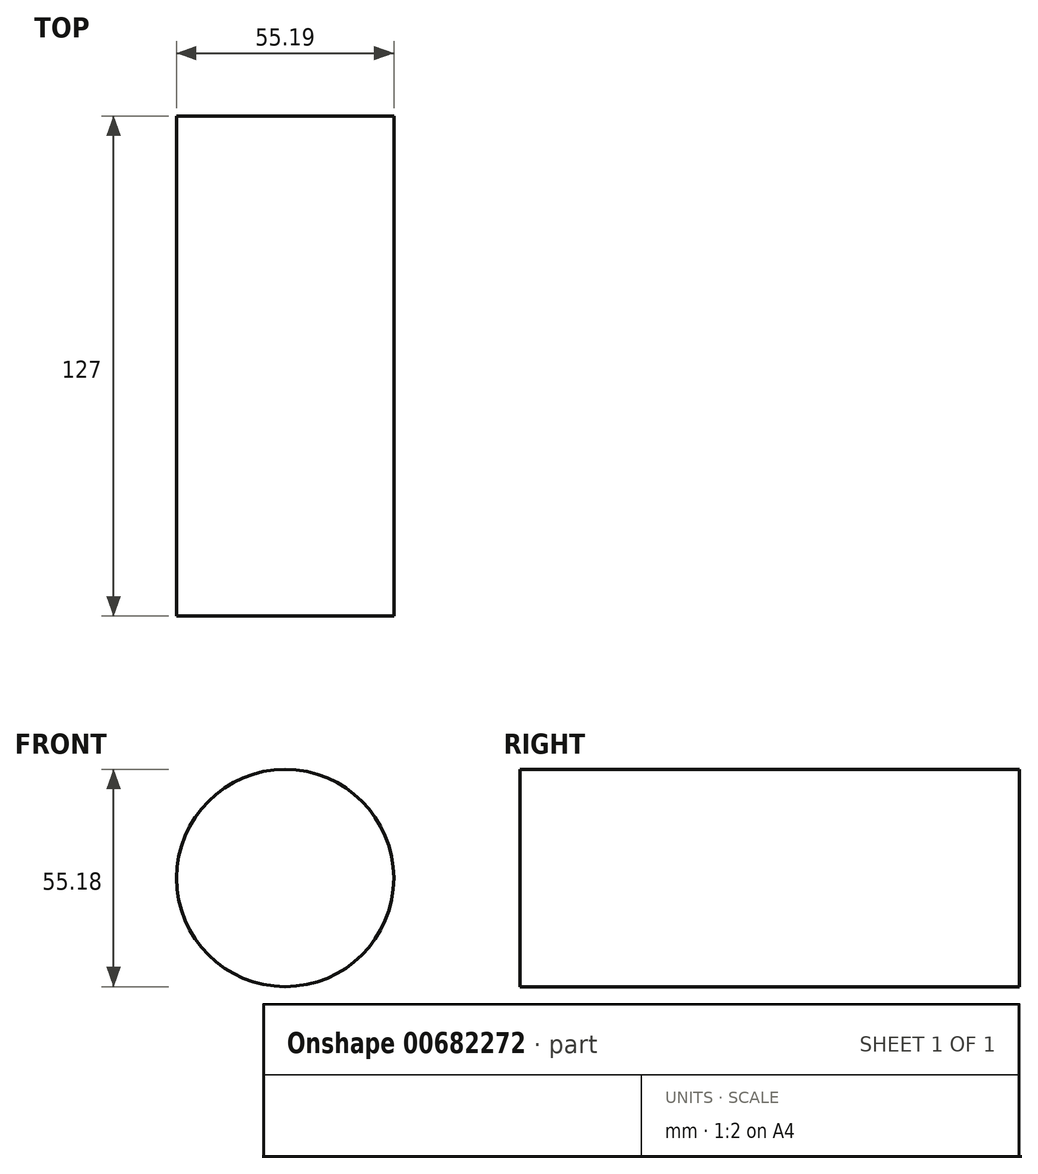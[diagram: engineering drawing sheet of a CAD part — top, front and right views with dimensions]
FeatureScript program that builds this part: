
annotation { "Feature Type Name" : "Feature", "Feature Type Description" : "" }
export const myFeature = defineFeature(function(context is Context, id is Id, definition is map)
    precondition{}
    {
        {
            var Q0;
            Q0=qCreatedBy(makeId("Front.planeOp"),FACE);
            var sketch = newSketch(context, id + "F0", { "sketchPlane" : qUnion([Q0])});
            skCircle(sketch, "E0", {"center": v(1.32, 0) * mm, "radius": 27.6 * mm});
            skSolve(sketch);
        }
        {
            var Q0;
            Q0=makeQuery(id+"F0.imprint","IMPRINT",FACE,{"disambiguationData":[TD([[makeQuery(id+"F0.imprint","IMPRINT",EDGE,{"derivedFrom":sQuery(id+"F0.wireOp",EDGE,"E0")}),1.0]])]});
            extrude(context, id + "F1", {"entities" : qUnion([Q0]), "depth" : 127 * mm, "offsetDistance" : 25.4 * mm});
        }
    });
